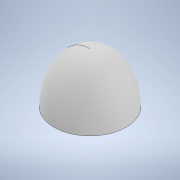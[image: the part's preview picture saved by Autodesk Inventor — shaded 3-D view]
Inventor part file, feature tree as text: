
AUTODESK INVENTOR PART (.ipt)
format: ipt  version: 2022 (Build 260153000, 153)  size: 250,880 bytes
history: native  units: in
note: dims shown in document units (in); Inventor stores cm internally (conversion verified against a paired STEP export)
features: sketch x3, revolve x1, thicken_offset x1, shell x1, extrude x1
ambient origin geometry x8: Origin, YZ Plane, XZ Plane, XY Plane, X Axis, Y Axis, Z Axis, Center Point
bodies: Solid1 (feature_tree)
feature tree (7):
  revolve  "Revolution1"  [1 undecoded]
  thicken_offset  "Thicken1"
  shell  "Shell2"  Thickness=0.25in
  extrude  "Extrusion1"  Depth=2.2in
  sketch  "Sketch3"  dims[d4=0.0344in]
  sketch  "Sketch1"  dims[d3=90.0deg d5=0.26in d6=0.25in d7=0.25in]
  sketch  "Sketch2"  dims[d10=0.25in d11=0.0in d12=2.2in]
note: 1 required parameter value undecoded (feature->parameter linkage not recoverable at this tier; creation-order binding heuristic only, values carry confidence <= 0.55)
